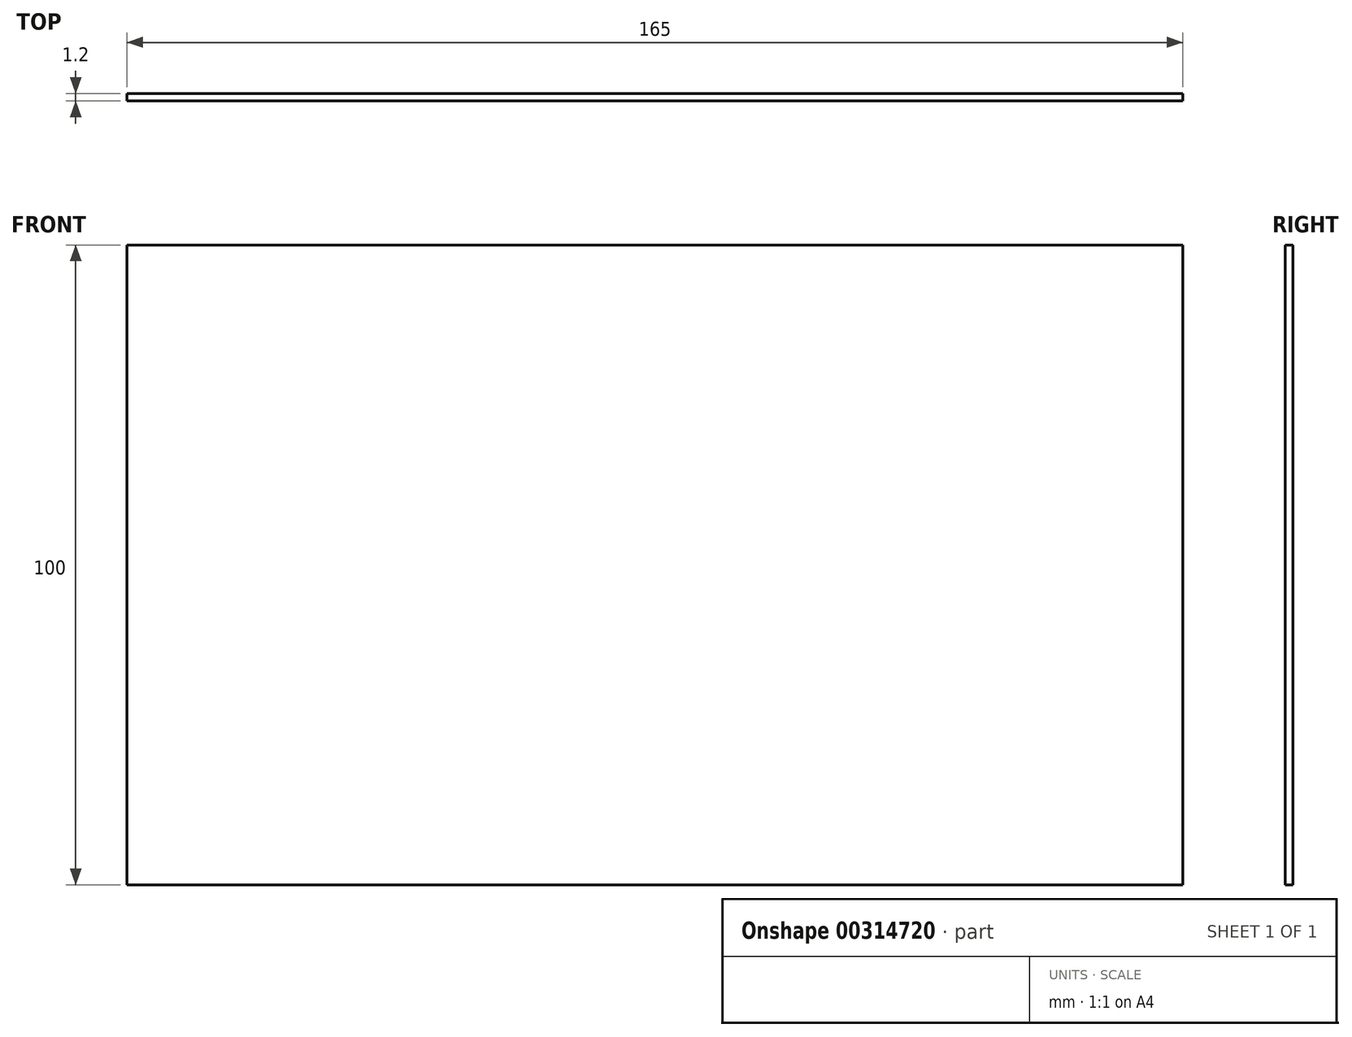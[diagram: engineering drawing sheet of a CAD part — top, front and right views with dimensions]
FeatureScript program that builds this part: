
annotation { "Feature Type Name" : "Feature", "Feature Type Description" : "" }
export const myFeature = defineFeature(function(context is Context, id is Id, definition is map)
    precondition{}
    {
        {
            var Q0;
            Q0=qCreatedBy(makeId("Front.planeOp"),FACE);
            var sketch = newSketch(context, id + "F0", { "sketchPlane" : qUnion([Q0])});
            skLineSegment(sketch, "E0.bottom", {"start": v(82.5, -50) * mm, "end": v(-82.5, -50) * mm});
            skLineSegment(sketch, "E0.top", {"start": v(82.5, 50) * mm, "end": v(-82.5, 50) * mm});
            skLineSegment(sketch, "E0.left", {"start": v(82.5, -50) * mm, "end": v(82.5, 50) * mm});
            skLineSegment(sketch, "E0.right", {"start": v(-82.5, -50) * mm, "end": v(-82.5, 50) * mm});
            skPoint(sketch, "E0.middle", {"position": v(0, 0) * mm});
            skSolve(sketch);
        }
        {
            var Q0;
            Q0=makeQuery(id+"F0.imprint","IMPRINT",FACE,{"disambiguationData":[TD([[makeQuery(id+"F0.imprint","IMPRINT",EDGE,{"derivedFrom":sQuery(id+"F0.wireOp",EDGE,"E0.bottom")}),-1.0]])]});
            extrude(context, id + "F1", {"entities" : qUnion([Q0]), "depth" : 1.2 * mm});
        }
    });
